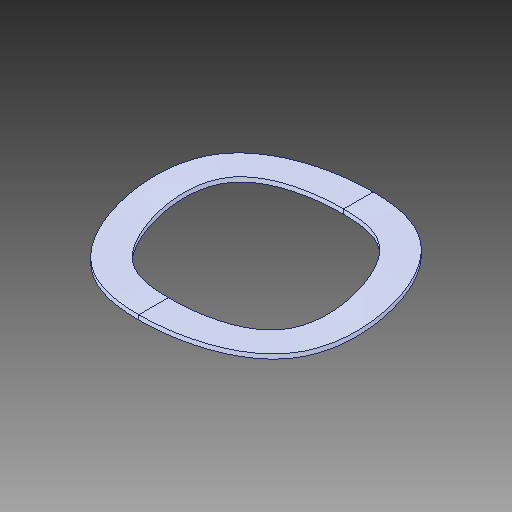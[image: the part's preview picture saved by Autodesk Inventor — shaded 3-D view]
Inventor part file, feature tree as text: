
AUTODESK INVENTOR PART (.ipt)
format: ipt  version: 2017 (Build 210142000, 142)  size: 115,200 bytes
history: native  units: in
note: dims shown in document units (in); Inventor stores cm internally (conversion verified against a paired STEP export)
features: loft x1
ambient origin geometry x8: Origin, YZ Plane, XZ Plane, XY Plane, X Axis, Y Axis, Z Axis, Center Point
bodies: Solid1 (feature_tree)
feature tree (1):
  loft  "Loft1"
